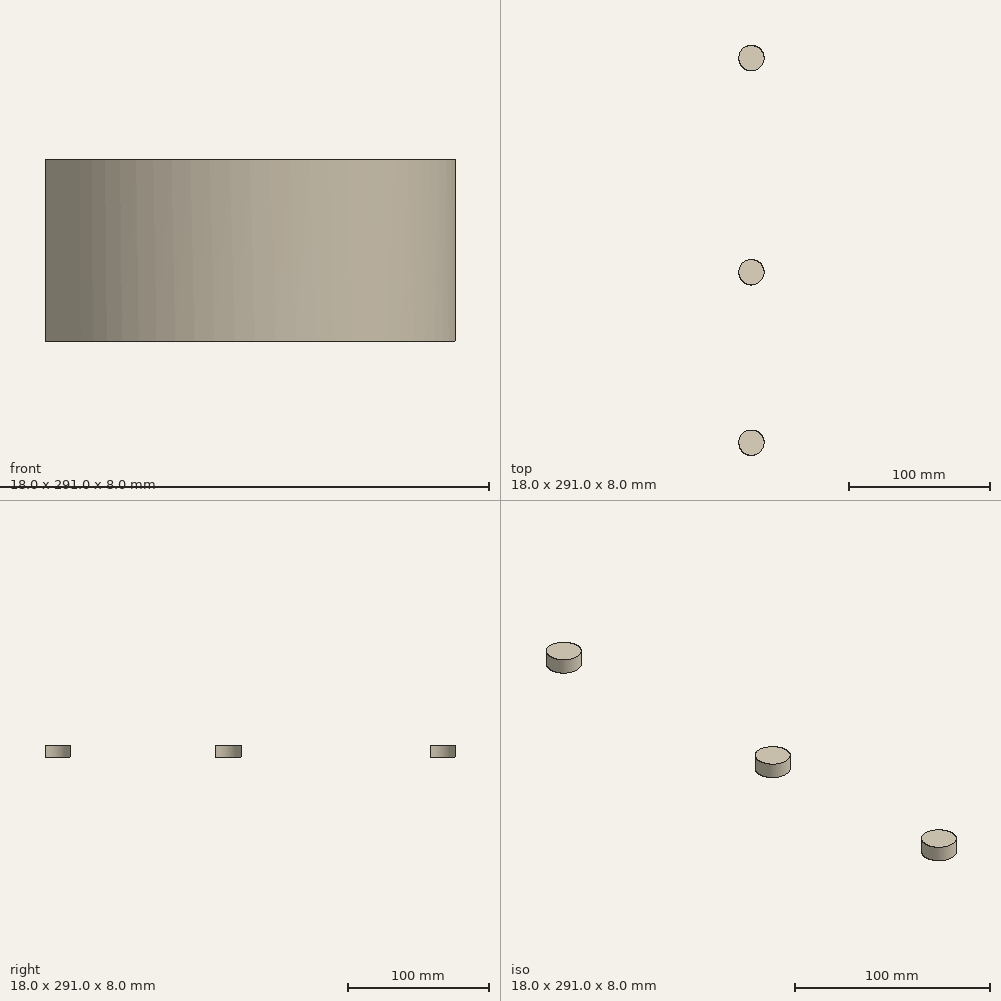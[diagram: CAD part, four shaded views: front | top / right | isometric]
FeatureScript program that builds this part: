
annotation { "Feature Type Name" : "Feature", "Feature Type Description" : "" }
export const myFeature = defineFeature(function(context is Context, id is Id, definition is map)
    precondition{}
    {
        {
            var Q0;
            Q0=qCreatedBy(makeId("Front.planeOp"),FACE);
            var sketch = newSketch(context, id + "F0", { "sketchPlane" : qUnion([Q0])});
            skLineSegment(sketch, "E0", {"start": v(0, 80) * mm, "end": v(0, 0) * mm});
            skLineSegment(sketch, "E1", {"start": v(0, 0) * mm, "end": v(80, 0) * mm});
            skLineSegment(sketch, "E2.0", {"start": v(18, 8) * mm, "end": v(75, 8) * mm});
            skLineSegment(sketch, "E2.1", {"start": v(8, 75) * mm, "end": v(8, 18) * mm});
            skLineSegment(sketch, "E3", {"start": v(0, 80) * mm, "end": v(3, 80) * mm});
            skLineSegment(sketch, "E4", {"start": v(80, 3) * mm, "end": v(80, 0) * mm});
            skPoint(sketch, "E5.visualSharp", {"position": v(8, 8) * mm});
            skArc(sketch, "E5.filletArc", {"start": v(8, 18) * mm, "mid": v(10.93, 10.93) * mm, "end": v(18, 8) * mm});
            skPoint(sketch, "E6.visualSharp", {"position": v(8, 80) * mm});
            skArc(sketch, "E6.filletArc", {"start": v(8, 75) * mm, "mid": v(6.54, 78.54) * mm, "end": v(3, 80) * mm});
            skPoint(sketch, "E7.visualSharp", {"position": v(80, 8) * mm});
            skArc(sketch, "E7.filletArc", {"start": v(80, 3) * mm, "mid": v(78.54, 6.54) * mm, "end": v(75, 8) * mm});
            skSolve(sketch);
        }
        {
            var Q0;
            Q0=makeQuery(id+"F0.imprint","IMPRINT",FACE,{"disambiguationData":[TD([[makeQuery(id+"F0.imprint","IMPRINT",EDGE,{"derivedFrom":sQuery(id+"F0.wireOp",EDGE,"E0")}),1.0]])]});
            extrude(context, id + "F1", {"entities" : qUnion([Q0]), "depth" : 770 * mm, "offsetDistance" : 25 * mm});
        }
        {
            var Q0;
            Q0=makeQuery(id+"F1.opExtrude","SWEPT_FACE",FACE,{"disambiguationData":[OSD([sQuery(id+"F0.wireOp",EDGE,"E1")])]});
            var sketch = newSketch(context, id + "F2", { "sketchPlane" : qUnion([Q0])});
            skLineSegment(sketch, "E8.0", {"start": v(0, 0) * mm, "end": v(80, 0) * mm});
            skLineSegment(sketch, "E9.0", {"start": v(80, 770) * mm, "end": v(80, 0) * mm});
            skLineSegment(sketch, "E10", {"start": v(80, 385) * mm, "end": v(45, 385) * mm});
            skLineSegment(sketch, "E11.0", {"start": v(80, 309) * mm, "end": v(45, 309) * mm});
            skLineSegment(sketch, "E12.0", {"start": v(80, 157) * mm, "end": v(45, 157) * mm});
            skLineSegment(sketch, "E13.0", {"start": v(80, 36) * mm, "end": v(45, 36) * mm});
            skCircle(sketch, "E14", {"center": v(45, 309) * mm, "radius": 9 * mm});
            skCircle(sketch, "E15", {"center": v(45, 157) * mm, "radius": 9 * mm});
            skCircle(sketch, "E16", {"center": v(45, 36) * mm, "radius": 9 * mm});
            skCircle(sketch, "E17.MirrorC", {"center": v(45, 461) * mm, "radius": 9 * mm});
            skCircle(sketch, "E18.MirrorC", {"center": v(45, 613) * mm, "radius": 9 * mm});
            skCircle(sketch, "E19.MirrorC", {"center": v(45, 734) * mm, "radius": 9 * mm});
            skSolve(sketch);
        }
        {
            var Q0;
            Q0=makeQuery(id+"F2.imprint","IMPRINT",FACE,{"disambiguationData":[TD([[makeQuery(id+"F2.imprint","IMPRINT",EDGE,{"derivedFrom":sQuery(id+"F2.wireOp",EDGE,"E16")}),1.0]])]});
            var Q1;
            Q1=makeQuery(id+"F2.imprint","IMPRINT",FACE,{"disambiguationData":[TD([[makeQuery(id+"F2.imprint","IMPRINT",EDGE,{"derivedFrom":sQuery(id+"F2.wireOp",EDGE,"E15")}),1.0]])]});
            var Q2;
            Q2=makeQuery(id+"F2.imprint","IMPRINT",FACE,{"disambiguationData":[TD([[makeQuery(id+"F2.imprint","IMPRINT",EDGE,{"derivedFrom":sQuery(id+"F2.wireOp",EDGE,"E14")}),1.0]])]});
            var Q3;
            Q3=makeQuery(id+"F2.imprint","IMPRINT",FACE,{"disambiguationData":[TD([[makeQuery(id+"F2.imprint","IMPRINT",EDGE,{"derivedFrom":sQuery(id+"F2.wireOp",EDGE,"E17.MirrorC")}),-1.0]])]});
            var Q4;
            Q4=makeQuery(id+"F2.imprint","IMPRINT",FACE,{"disambiguationData":[TD([[makeQuery(id+"F2.imprint","IMPRINT",EDGE,{"derivedFrom":sQuery(id+"F2.wireOp",EDGE,"E18.MirrorC")}),-1.0]])]});
            var Q5;
            Q5=makeQuery(id+"F2.imprint","IMPRINT",FACE,{"disambiguationData":[TD([[makeQuery(id+"F2.imprint","IMPRINT",EDGE,{"derivedFrom":sQuery(id+"F2.wireOp",EDGE,"E19.MirrorC")}),-1.0]])]});
            extrude(context, id + "F3", {"entities" : qUnion([Q0, Q1, Q2, Q3, Q4, Q5]), "operationType" : NewBodyOperationType.REMOVE, "endBound" : BoundingType.UP_TO_NEXT, "oppositeDirection" : true, "depth" : 25 * mm, "offsetDistance" : 25 * mm});
        }
    });
